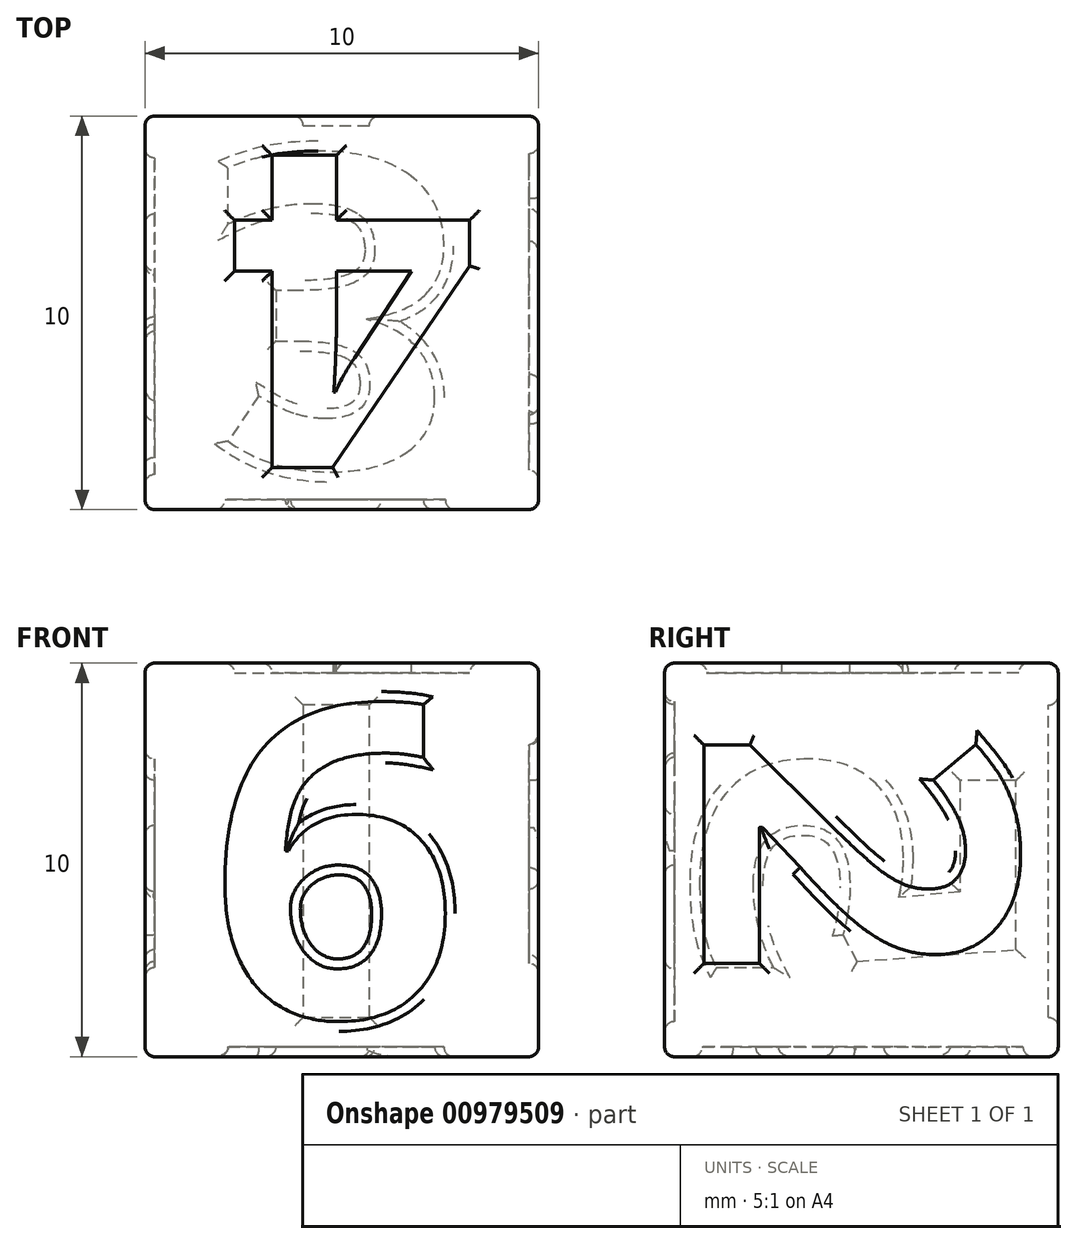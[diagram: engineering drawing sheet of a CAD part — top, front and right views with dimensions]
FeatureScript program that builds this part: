
annotation { "Feature Type Name" : "Feature", "Feature Type Description" : "" }
export const myFeature = defineFeature(function(context is Context, id is Id, definition is map)
    precondition{}
    {
        {
            var Q0;
            Q0=qCreatedBy(makeId("Top.planeOp"),FACE);
            var sketch = newSketch(context, id + "F0", { "sketchPlane" : qUnion([Q0])});
            skLineSegment(sketch, "E0.bottom", {"start": v(5, 5) * mm, "end": v(-5, 5) * mm});
            skLineSegment(sketch, "E0.top", {"start": v(5, -5) * mm, "end": v(-5, -5) * mm});
            skLineSegment(sketch, "E0.left", {"start": v(5, 5) * mm, "end": v(5, -5) * mm});
            skLineSegment(sketch, "E0.right", {"start": v(-5, 5) * mm, "end": v(-5, -5) * mm});
            skPoint(sketch, "E0.middle", {"position": v(0, 0) * mm});
            skSolve(sketch);
        }
        {
            var Q0;
            Q0=makeQuery(id+"F0.imprint","IMPRINT",FACE,{"disambiguationData":[TD([[makeQuery(id+"F0.imprint","IMPRINT",EDGE,{"derivedFrom":sQuery(id+"F0.wireOp",EDGE,"E0.bottom")}),1.0]])]});
            extrude(context, id + "F1", {"entities" : qUnion([Q0]), "depth" : 10 * mm, "offsetDistance" : 25 * mm});
        }
        {
            var Q0;
            Q0=makeQuery(id+"F1.opExtrude","CAP_FACE",FACE,{"disambiguationData":[OSD([sQuery(id+"F0.wireOp",EDGE,"E0.bottom"),sQuery(id+"F0.wireOp",EDGE,"E0.top"),sQuery(id+"F0.wireOp",EDGE,"E0.left"),sQuery(id+"F0.wireOp",EDGE,"E0.right")])],"isStart":false});
            var sketch = newSketch(context, id + "F2", { "sketchPlane" : qUnion([Q0])});
            skLineSegment(sketch, "E1", {"start": v(0, 4) * mm, "end": v(0, 5) * mm, "construction": true});
            skLineSegment(sketch, "E2", {"start": v(-3.44, 0) * mm, "end": v(-5, 0) * mm, "construction": true});
            skLineSegment(sketch, "E3", {"start": v(0, -4) * mm, "end": v(0, -5) * mm, "construction": true});
            skLineSegment(sketch, "E4", {"start": v(3.44, 0) * mm, "end": v(5, 0) * mm, "construction": true});
            skText(sketch, "E5", { "text": "4", "fontName": "OpenSans-Bold.ttf"});
            const initialGuessF2  = {"E5": [0.00344, 0.004, -1, 0, 0.008]};
            skSetInitialGuess(sketch, initialGuessF2);
            skSolve(sketch);
        }
        {
            var Q0;
            Q0=makeQuery(id+"F2.imprint","IMPRINT",FACE,{"disambiguationData":[TD([[makeQuery(id+"F2.imprint","IMPRINT",EDGE,{"derivedFrom":sQuery(id+"F2.wireOp",EDGE,"E5.sketch_text.stroke-0")}),-1.0]])]});
            extrude(context, id + "F3", {"entities" : qUnion([Q0]), "operationType" : NewBodyOperationType.REMOVE, "oppositeDirection" : true, "depth" : .25 * mm, "offsetDistance" : 25 * mm});
        }
        {
            var Q0;
            Q0=makeQuery(id+"F1.opExtrude","SWEPT_FACE",FACE,{"disambiguationData":[OSD([sQuery(id+"F0.wireOp",EDGE,"E0.left")])]});
            var sketch = newSketch(context, id + "F4", { "sketchPlane" : qUnion([Q0])});
            skText(sketch, "E6", { "text": "2", "fontName": "OpenSans-Bold.ttf"});
            skLineSegment(sketch, "E7", {"start": v(0, 8.36) * mm, "end": v(0, 10) * mm, "construction": true});
            skLineSegment(sketch, "E8", {"start": v(4, 5) * mm, "end": v(5, 5) * mm, "construction": true});
            skLineSegment(sketch, "E9", {"start": v(0, 1.64) * mm, "end": v(0, 0) * mm, "construction": true});
            skLineSegment(sketch, "E10", {"start": v(-4, 5) * mm, "end": v(-5, 5) * mm, "construction": true});
            const initialGuessF4  = {"E6": [-0.004, 0.00836, 0, -1, 0.008]};
            skSetInitialGuess(sketch, initialGuessF4);
            skSolve(sketch);
        }
        {
            var Q0;
            Q0=makeQuery(id+"F4.imprint","IMPRINT",FACE,{"disambiguationData":[TD([[makeQuery(id+"F4.imprint","IMPRINT",EDGE,{"derivedFrom":sQuery(id+"F4.wireOp",EDGE,"E6.sketch_text.stroke-0")}),-1.0]])]});
            extrude(context, id + "F5", {"entities" : qUnion([Q0]), "operationType" : NewBodyOperationType.REMOVE, "oppositeDirection" : true, "depth" : .25 * mm, "offsetDistance" : 25 * mm});
        }
        {
            var Q0;
            Q0=makeQuery(id+"F1.opExtrude","CAP_FACE",FACE,{"disambiguationData":[OSD([sQuery(id+"F0.wireOp",EDGE,"E0.bottom"),sQuery(id+"F0.wireOp",EDGE,"E0.top"),sQuery(id+"F0.wireOp",EDGE,"E0.left"),sQuery(id+"F0.wireOp",EDGE,"E0.right")])],"isStart":true});
            var sketch = newSketch(context, id + "F6", { "sketchPlane" : qUnion([Q0])});
            skText(sketch, "E11", { "text": "3", "fontName": "OpenSans-Bold.ttf"});
            skLineSegment(sketch, "E12", {"start": v(0, -4) * mm, "end": v(0, -5) * mm, "construction": true});
            skLineSegment(sketch, "E13", {"start": v(3.32, 0) * mm, "end": v(5, 0) * mm, "construction": true});
            skLineSegment(sketch, "E14", {"start": v(-3.32, 0) * mm, "end": v(-5, 0) * mm, "construction": true});
            skPoint(sketch, "E15", {"position": v(0, 0) * mm});
            skLineSegment(sketch, "E16", {"start": v(0, 4) * mm, "end": v(0, 5) * mm, "construction": true});
            const initialGuessF6  = {"E11": [-0.00332, -0.004, 1, 0, 0.008]};
            skSetInitialGuess(sketch, initialGuessF6);
            skSolve(sketch);
        }
        {
            var Q0;
            Q0=makeQuery(id+"F6.imprint","IMPRINT",FACE,{"disambiguationData":[TD([[makeQuery(id+"F6.imprint","IMPRINT",EDGE,{"derivedFrom":sQuery(id+"F6.wireOp",EDGE,"E11.sketch_text.stroke-0")}),-1.0]])]});
            extrude(context, id + "F7", {"entities" : qUnion([Q0]), "operationType" : NewBodyOperationType.REMOVE, "oppositeDirection" : true, "depth" : .25 * mm, "offsetDistance" : 25 * mm});
        }
        {
            var Q0;
            Q0=makeQuery(id+"F1.opExtrude","SWEPT_FACE",FACE,{"disambiguationData":[OSD([sQuery(id+"F0.wireOp",EDGE,"E0.right")])]});
            var sketch = newSketch(context, id + "F8", { "sketchPlane" : qUnion([Q0])});
            skLineSegment(sketch, "E17", {"start": v(-4, 5) * mm, "end": v(-5, 5) * mm, "construction": true});
            skPoint(sketch, "E18.endSnap0", {"position": v(5, 5) * mm});
            skLineSegment(sketch, "E19", {"start": v(0, 1.72) * mm, "end": v(0, 0) * mm, "construction": true});
            skLineSegment(sketch, "E20", {"start": v(0, 8.28) * mm, "end": v(0, 10) * mm, "construction": true});
            skLineSegment(sketch, "E21", {"start": v(5, 5) * mm, "end": v(4, 5) * mm, "construction": true});
            skText(sketch, "E22", { "text": "5", "fontName": "OpenSans-Bold.ttf"});
            const initialGuessF8  = {"E22": [0.004, 0.00172, 0, 1, 0.008]};
            skSetInitialGuess(sketch, initialGuessF8);
            skSolve(sketch);
        }
        {
            var Q0;
            Q0=makeQuery(id+"F8.imprint","IMPRINT",FACE,{"disambiguationData":[TD([[makeQuery(id+"F8.imprint","IMPRINT",EDGE,{"derivedFrom":sQuery(id+"F8.wireOp",EDGE,"E22.sketch_text.stroke-0")}),-1.0]])]});
            extrude(context, id + "F9", {"entities" : qUnion([Q0]), "operationType" : NewBodyOperationType.REMOVE, "oppositeDirection" : true, "depth" : .25 * mm, "offsetDistance" : 25 * mm});
        }
        {
            var Q0;
            Q0=makeQuery(id+"F1.opExtrude","SWEPT_FACE",FACE,{"disambiguationData":[OSD([sQuery(id+"F0.wireOp",EDGE,"E0.bottom")])]});
            var sketch = newSketch(context, id + "F10", { "sketchPlane" : qUnion([Q0])});
            skText(sketch, "E23", { "text": "I", "fontName": "OpenSans-Bold.ttf"});
            skLineSegment(sketch, "E24", {"start": v(5, 5) * mm, "end": v(1.7, 5) * mm, "construction": true});
            skLineSegment(sketch, "E25", {"start": v(0, 0) * mm, "end": v(0, 1) * mm, "construction": true});
            skLineSegment(sketch, "E26", {"start": v(-5, 5) * mm, "end": v(-1.7, 5) * mm, "construction": true});
            skLineSegment(sketch, "E27", {"start": v(0, 10) * mm, "end": v(0, 9) * mm, "construction": true});
            const initialGuessF10  = {"E23": [-0.0017, 0.001, 1, 0, 0.008]};
            skSetInitialGuess(sketch, initialGuessF10);
            skSolve(sketch);
        }
        {
            var Q0;
            Q0=makeQuery(id+"F10.imprint","IMPRINT",FACE,{"disambiguationData":[TD([[makeQuery(id+"F10.imprint","IMPRINT",EDGE,{"derivedFrom":sQuery(id+"F10.wireOp",EDGE,"E23.sketch_text.stroke-0")}),-1.0]])]});
            extrude(context, id + "F11", {"entities" : qUnion([Q0]), "operationType" : NewBodyOperationType.REMOVE, "oppositeDirection" : true, "depth" : .25 * mm, "offsetDistance" : 25 * mm});
        }
        {
            var Q0;
            Q0=makeQuery(id+"F1.opExtrude","SWEPT_FACE",FACE,{"disambiguationData":[OSD([sQuery(id+"F0.wireOp",EDGE,"E0.top")])]});
            var sketch = newSketch(context, id + "F12", { "sketchPlane" : qUnion([Q0])});
            skText(sketch, "E28", { "text": "6", "fontName": "OpenSans-Bold.ttf"});
            skLineSegment(sketch, "E29", {"start": v(-5, 5) * mm, "end": v(-3.36, 5) * mm, "construction": true});
            skLineSegment(sketch, "E30", {"start": v(0, 10) * mm, "end": v(0, 9) * mm, "construction": true});
            skLineSegment(sketch, "E31", {"start": v(5, 5) * mm, "end": v(3.36, 5) * mm, "construction": true});
            skLineSegment(sketch, "E32", {"start": v(0, 0) * mm, "end": v(0, 1) * mm, "construction": true});
            const initialGuessF12  = {"E28": [-0.00336, 0.001, 1, 0, 0.008]};
            skSetInitialGuess(sketch, initialGuessF12);
            skSolve(sketch);
        }
        {
            var Q0;
            Q0=makeQuery(id+"F12.imprint","IMPRINT",FACE,{"disambiguationData":[TD([[makeQuery(id+"F12.imprint","IMPRINT",EDGE,{"derivedFrom":sQuery(id+"F12.wireOp",EDGE,"E28.sketch_text.stroke-0")}),-1.0]])]});
            extrude(context, id + "F13", {"entities" : qUnion([Q0]), "operationType" : NewBodyOperationType.REMOVE, "oppositeDirection" : true, "depth" : .25 * mm, "offsetDistance" : 25 * mm});
        }
        {
            var Q0;
            Q0=makeQuery(id+"F1.opExtrude","CAP_EDGE",EDGE,{"disambiguationData":[OSD([sQuery(id+"F0.wireOp",EDGE,"E0.bottom")])],"isStart":false});
            var Q1;
            Q1=makeQuery(id+"F1.opExtrude","CAP_EDGE",EDGE,{"disambiguationData":[OSD([sQuery(id+"F0.wireOp",EDGE,"E0.right")])],"isStart":false});
            var Q2;
            {var subQ0=sQuery(id+"F0.wireOp",EDGE,"E0.left");var subQ1=sQuery(id+"F0.wireOp",EDGE,"E0.bottom");var subQ2=sQuery(id+"F0.wireOp",EDGE,"E0.right");var subQ3=sQuery(id+"F0.wireOp",EDGE,"E0.top");Q2=makeQuery(id+"F3.boolean.opBoolean","SPLIT",FACE,{"disambiguationData":[TD([makeQuery(id+"F1.opExtrude","SWEPT_FACE",FACE,{"disambiguationData":[OSD([subQ1])]})])],"derivedFrom":makeQuery(id+"F1.opExtrude","CAP_FACE",FACE,{"disambiguationData":[OSD([subQ1,subQ3,subQ0,subQ2])],"isStart":false})});}
            var Q3;
            Q3=makeQuery(id+"F3.boolean.opBoolean","COPY",EDGE,{"derivedFrom":makeQuery(id+"F3.opExtrude","CAP_EDGE",EDGE,{"disambiguationData":[OSD([sQuery(id+"F2.wireOp",EDGE,"E5.sketch_text.stroke-15")])],"isStart":true})});
            var Q4;
            Q4=makeQuery(id+"F3.boolean.opBoolean","COPY",EDGE,{"derivedFrom":makeQuery(id+"F3.opExtrude","CAP_EDGE",EDGE,{"disambiguationData":[OSD([sQuery(id+"F2.wireOp",EDGE,"E5.sketch_text.stroke-13")])],"isStart":true})});
            var Q5;
            Q5=makeQuery(id+"F3.boolean.opBoolean","COPY",EDGE,{"derivedFrom":makeQuery(id+"F3.opExtrude","CAP_EDGE",EDGE,{"disambiguationData":[OSD([sQuery(id+"F2.wireOp",EDGE,"E5.sketch_text.stroke-17")])],"isStart":true})});
            var Q6;
            {var subQ1=sQuery(id+"F0.wireOp",EDGE,"E0.left");var subQ2=sQuery(id+"F0.wireOp",EDGE,"E0.top");Q6=makeQuery(id+"F13.boolean.opBoolean","SPLIT",FACE,{"disambiguationData":[TD([makeQuery(id+"F1.opExtrude","SWEPT_FACE",FACE,{"disambiguationData":[OSD([subQ1])]})])],"derivedFrom":makeQuery(id+"F1.opExtrude","SWEPT_FACE",FACE,{"disambiguationData":[OSD([subQ2])]})});}
            var Q7;
            Q7=makeQuery(id+"F13.boolean.opBoolean","SPLIT",FACE,{"disambiguationData":[TD([makeQuery(id+"F13.opExtrude","SWEPT_FACE",FACE,{"disambiguationData":[OSD([sQuery(id+"F12.wireOp",EDGE,"E28.sketch_text.stroke-17")])]})])],"derivedFrom":makeQuery(id+"F1.opExtrude","SWEPT_FACE",FACE,{"disambiguationData":[OSD([sQuery(id+"F0.wireOp",EDGE,"E0.top")])]})});
            var Q8;
            Q8=makeQuery(id+"F1.opExtrude","SWEPT_FACE",FACE,{"disambiguationData":[OSD([sQuery(id+"F0.wireOp",EDGE,"E0.right")])]});
            var Q9;
            Q9=makeQuery(id+"F1.opExtrude","SWEPT_FACE",FACE,{"disambiguationData":[OSD([sQuery(id+"F0.wireOp",EDGE,"E0.bottom")])]});
            var Q10;
            Q10=makeQuery(id+"F1.opExtrude","CAP_FACE",FACE,{"disambiguationData":[OSD([sQuery(id+"F0.wireOp",EDGE,"E0.bottom"),sQuery(id+"F0.wireOp",EDGE,"E0.top"),sQuery(id+"F0.wireOp",EDGE,"E0.left"),sQuery(id+"F0.wireOp",EDGE,"E0.right")])],"isStart":true});
            var Q11;
            Q11=makeQuery(id+"F1.opExtrude","SWEPT_FACE",FACE,{"disambiguationData":[OSD([sQuery(id+"F0.wireOp",EDGE,"E0.left")])]});
            fillet(context, id + "F14", {"entities" : qUnion([Q0, Q1, Q2, Q3, Q4, Q5, Q6, Q7, Q8, Q9, Q10, Q11]), "radius" : .25 * mm, "tangentPropagation" : true, "allowEdgeOverflow" : false});
        }
    });
